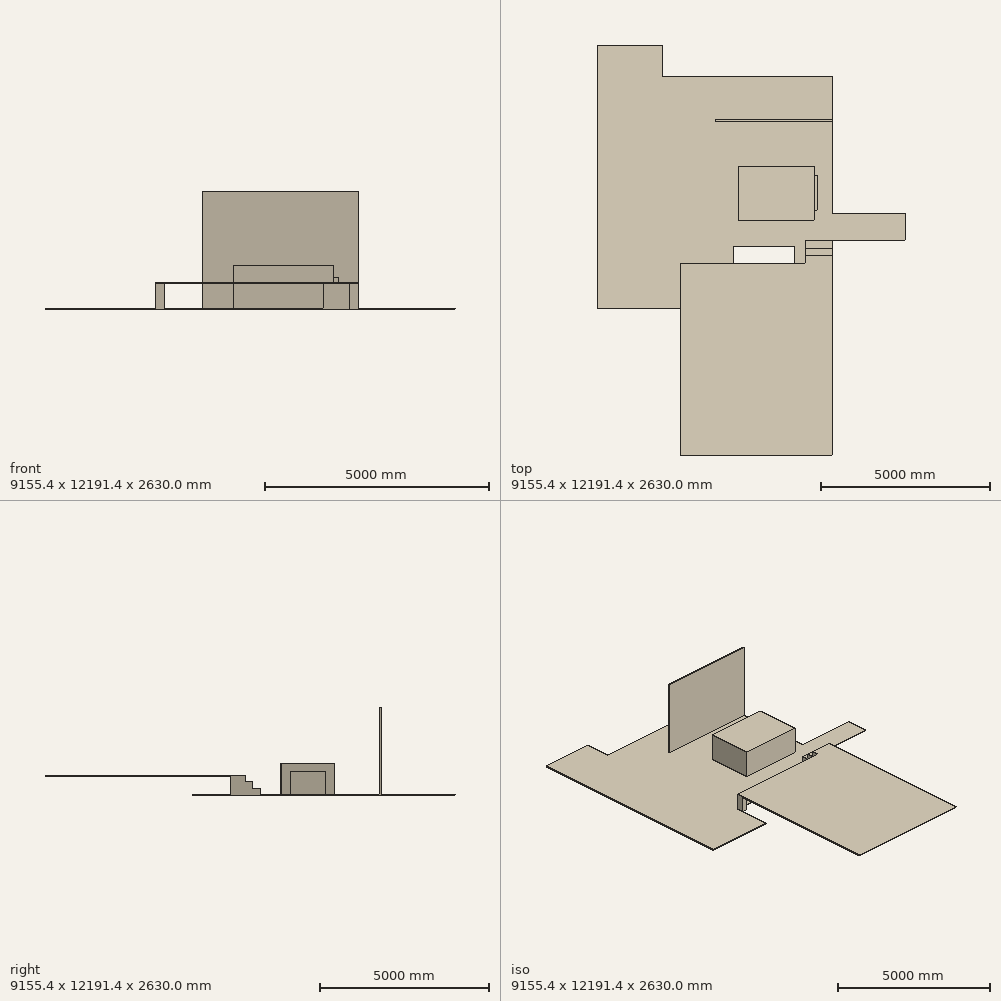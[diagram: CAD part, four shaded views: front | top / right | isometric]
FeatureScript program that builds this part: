
annotation { "Feature Type Name" : "Feature", "Feature Type Description" : "" }
export const myFeature = defineFeature(function(context is Context, id is Id, definition is map)
    precondition{}
    {
        {
            var Q0;
            Q0=qCreatedBy(makeId("Top.planeOp"),FACE);
            var sketch = newSketch(context, id + "F0", { "sketchPlane" : qUnion([Q0])});
            skLineSegment(sketch, "E0.bottom", {"start": v(-1125, 800) * mm, "end": v(1125, 800) * mm});
            skLineSegment(sketch, "E0.top", {"start": v(-1125, -800) * mm, "end": v(1125, -800) * mm});
            skLineSegment(sketch, "E0.left", {"start": v(-1125, 800) * mm, "end": v(-1125, -800) * mm});
            skLineSegment(sketch, "E0.right", {"start": v(1125, 800) * mm, "end": v(1125, -800) * mm});
            skPoint(sketch, "E0.middle", {"position": v(0, 0) * mm});
            skLineSegment(sketch, "E1.bottom", {"start": v(3.09, 2130) * mm, "end": v(-1796.91, 2130) * mm});
            skLineSegment(sketch, "E2", {"start": v(1675, 3460) * mm, "end": v(1675, -610) * mm});
            skLineSegment(sketch, "E3", {"start": v(1675, -610) * mm, "end": v(3053.14, -610) * mm});
            skLineSegment(sketch, "E4", {"start": v(3053.14, -610) * mm, "end": v(3053.14, 361.12) * mm});
            skLineSegment(sketch, "E5", {"start": v(3053.14, 361.12) * mm, "end": v(3843.14, 361.12) * mm});
            skLineSegment(sketch, "E6", {"start": v(3843.14, -1400) * mm, "end": v(2516.8, -1400) * mm});
            skLineSegment(sketch, "E7", {"start": v(2516.8, -1400) * mm, "end": v(2516.8, -3015.82) * mm});
            skLineSegment(sketch, "E8", {"start": v(2516.8, -3015.82) * mm, "end": v(1817.51, -3015.82) * mm});
            skLineSegment(sketch, "E9", {"start": v(1817.51, -3015.82) * mm, "end": v(1817.51, -1400) * mm});
            skLineSegment(sketch, "E10", {"start": v(1817.51, -1400) * mm, "end": v(1675, -1400) * mm});
            skLineSegment(sketch, "E11", {"start": v(1675, -1400) * mm, "end": v(1675, -2100) * mm});
            skLineSegment(sketch, "E12", {"start": v(1675, -2100) * mm, "end": v(885, -2100) * mm});
            skLineSegment(sketch, "E13", {"start": v(885, -2100) * mm, "end": v(885, -1400) * mm});
            skLineSegment(sketch, "E14", {"start": v(885, -2100) * mm, "end": v(-2855.91, -2100) * mm});
            skLineSegment(sketch, "E15", {"start": v(885, -1400) * mm, "end": v(1675, -1400) * mm});
            skLineSegment(sketch, "E16", {"start": v(1675, -1400) * mm, "end": v(1675, -1400) * mm});
            skLineSegment(sketch, "E17.bottom", {"start": v(-2855.91, -300) * mm, "end": v(-2355.91, -300) * mm});
            skLineSegment(sketch, "E17.top", {"start": v(-2855.91, -2100) * mm, "end": v(-2355.91, -2100) * mm});
            skLineSegment(sketch, "E17.left", {"start": v(-2855.91, -300) * mm, "end": v(-2855.91, -2100) * mm});
            skLineSegment(sketch, "E17.right", {"start": v(-2355.91, -300) * mm, "end": v(-2355.91, -2100) * mm});
            skLineSegment(sketch, "E18", {"start": v(2516.8, -1400) * mm, "end": v(1817.51, -1400) * mm});
            skLineSegment(sketch, "E19", {"start": v(3053.14, -610) * mm, "end": v(3843.14, -610) * mm});
            skLineSegment(sketch, "E20", {"start": v(3843.14, 361.12) * mm, "end": v(3843.14, -610) * mm});
            skLineSegment(sketch, "E21", {"start": v(3843.14, -610) * mm, "end": v(3843.14, -1400) * mm});
            skLineSegment(sketch, "E22", {"start": v(-2855.91, -2100) * mm, "end": v(-2855.91, -3422.45) * mm});
            skLineSegment(sketch, "E23", {"start": v(-2855.91, -3422.45) * mm, "end": v(-2855.91, -7802.65) * mm});
            skLineSegment(sketch, "E24", {"start": v(-2855.91, -7802.65) * mm, "end": v(1675, -7802.65) * mm});
            skLineSegment(sketch, "E25", {"start": v(1675, -7802.65) * mm, "end": v(1675, -2100) * mm});
            skLineSegment(sketch, "E26", {"start": v(-2855.91, -3422.45) * mm, "end": v(-5312.24, -3422.45) * mm});
            skLineSegment(sketch, "E27", {"start": v(-3375.14, 3460) * mm, "end": v(1675, 3460) * mm});
            skLineSegment(sketch, "E28.bottom", {"start": v(-1185.34, -3222.94) * mm, "end": v(110.16, -3222.94) * mm});
            skLineSegment(sketch, "E28.top", {"start": v(-1185.34, -6783.92) * mm, "end": v(110.16, -6783.92) * mm});
            skLineSegment(sketch, "E28.left", {"start": v(-1185.34, -3222.94) * mm, "end": v(-1185.34, -6783.92) * mm});
            skLineSegment(sketch, "E28.right", {"start": v(110.16, -3222.94) * mm, "end": v(110.16, -6783.92) * mm});
            skLineSegment(sketch, "E29.bottom", {"start": v(1675, 2130) * mm, "end": v(-1796.91, 2130) * mm});
            skLineSegment(sketch, "E29.top", {"start": v(1675, 2180) * mm, "end": v(-1796.91, 2180) * mm});
            skLineSegment(sketch, "E29.left", {"start": v(1675, 2130) * mm, "end": v(1675, 2180) * mm});
            skLineSegment(sketch, "E30", {"start": v(-1796.91, 2130) * mm, "end": v(-1796.91, 2180) * mm});
            skLineSegment(sketch, "E31", {"start": v(-3375.14, 3460) * mm, "end": v(-3375.14, 4402.44) * mm});
            skLineSegment(sketch, "E32", {"start": v(-3366, 4388.7) * mm, "end": v(-5312.24, 4388.7) * mm});
            skLineSegment(sketch, "E33", {"start": v(-5312.24, -3422.45) * mm, "end": v(-5312.24, 4388.7) * mm});
            skLineSegment(sketch, "E34.bottom", {"start": v(544.09, -2100) * mm, "end": v(-1255.91, -2100) * mm});
            skLineSegment(sketch, "E34.top", {"start": v(544.09, -1600) * mm, "end": v(-1255.91, -1600) * mm});
            skLineSegment(sketch, "E34.left", {"start": v(544.09, -2100) * mm, "end": v(544.09, -1600) * mm});
            skLineSegment(sketch, "E34.right", {"start": v(-1255.91, -2100) * mm, "end": v(-1255.91, -1600) * mm});
            skSolve(sketch);
        }
        {
            var Q0;
            Q0=makeQuery(id+"F0.imprint","IMPRINT",FACE,{"disambiguationData":[TD([[makeQuery(id+"F0.imprint","IMPRINT",EDGE,{"derivedFrom":sQuery(id+"F0.wireOp",EDGE,"E0.bottom")}),-1.0]])]});
            extrude(context, id + "F1", {"entities" : qUnion([Q0]), "depth" : 940 * mm});
        }
        {
            var Q0;
            Q0=makeQuery(id+"F0.imprint","IMPRINT",FACE,{"disambiguationData":[TD([[makeQuery(id+"F0.imprint","IMPRINT",EDGE,{"derivedFrom":sQuery(id+"F0.wireOp",EDGE,"E0.bottom")}),1.0]])]});
            var Q1;
            Q1=makeQuery(id+"F0.imprint","IMPRINT",FACE,{"disambiguationData":[TD([[makeQuery(id+"F0.imprint","IMPRINT",EDGE,{"derivedFrom":sQuery(id+"F0.wireOp",EDGE,"E1.top")}),-1.0]])]});
            var Q2;
            Q2=makeQuery(id+"F0.imprint","IMPRINT",FACE,{"disambiguationData":[TD([[makeQuery(id+"F0.imprint","IMPRINT",EDGE,{"derivedFrom":sQuery(id+"F0.wireOp",EDGE,"E17.bottom")}),-1.0]])]});
            var Q3;
            Q3=makeQuery(id+"F0.imprint","IMPRINT",FACE,{"disambiguationData":[TD([[makeQuery(id+"F0.imprint","IMPRINT",EDGE,{"derivedFrom":sQuery(id+"F0.wireOp",EDGE,"E11")}),-1.0]])]});
            var Q4;
            Q4=makeQuery(id+"F0.imprint","IMPRINT",FACE,{"disambiguationData":[TD([[makeQuery(id+"F0.imprint","IMPRINT",EDGE,{"derivedFrom":sQuery(id+"F0.wireOp",EDGE,"H7tPlg6k-jWhV-1Bwv-etl5-hqIqn9BFFYRF.bottom")}),1.0]])]});
            var Q5;
            Q5=makeQuery(id+"F0.imprint","IMPRINT",FACE,{"disambiguationData":[TD([[makeQuery(id+"F0.imprint","IMPRINT",EDGE,{"derivedFrom":sQuery(id+"F0.wireOp",EDGE,"qLvadJ40-6Qau-X74K-FQ8g-niZacNmFLS0U.bottom")}),1.0]])]});
            var Q6;
            Q6=makeQuery(id+"F0.imprint","IMPRINT",FACE,{"disambiguationData":[TD([[makeQuery(id+"F0.imprint","IMPRINT",EDGE,{"derivedFrom":sQuery(id+"F0.wireOp",EDGE,"E29.top")}),1.0]])]});
            var Q7;
            Q7=makeQuery(id+"F0.imprint","IMPRINT",FACE,{"disambiguationData":[TD([[makeQuery(id+"F0.imprint","IMPRINT",EDGE,{"derivedFrom":sQuery(id+"F0.wireOp",EDGE,"E0.bottom")}),-1.0]])]});
            var Q8;
            Q8=makeQuery(id+"F0.imprint","IMPRINT",FACE,{"disambiguationData":[TD([[makeQuery(id+"F0.imprint","IMPRINT",EDGE,{"derivedFrom":sQuery(id+"F0.wireOp",EDGE,"E34.bottom")}),-1.0]])]});
            extrude(context, id + "F2", {"entities" : qUnion([Q0, Q1, Q2, Q3, Q4, Q5, Q6, Q7, Q8]), "operationType" : NewBodyOperationType.ADD, "oppositeDirection" : true, "depth" : 30 * mm});
        }
        {
            var Q0;
            Q0=makeQuery(id+"F1.opExtrude","SWEPT_FACE",FACE,{"disambiguationData":[OSD([sQuery(id+"F0.wireOp",EDGE,"E0.right")])]});
            var sketch = newSketch(context, id + "F3", { "sketchPlane" : qUnion([Q0])});
            skLineSegment(sketch, "E35.bottom", {"start": v(-525, 0) * mm, "end": v(525, 0) * mm});
            skLineSegment(sketch, "E35.top", {"start": v(-525, 690) * mm, "end": v(525, 690) * mm});
            skLineSegment(sketch, "E35.left", {"start": v(-525, 0) * mm, "end": v(-525, 690) * mm});
            skLineSegment(sketch, "E35.right", {"start": v(525, 0) * mm, "end": v(525, 690) * mm});
            skPoint(sketch, "E36", {"position": v(0, 690) * mm});
            skSolve(sketch);
        }
        {
            var Q0;
            Q0=qSketchRegion(id+"F3",true);
            extrude(context, id + "F4", {"entities" : qUnion([Q0]), "operationType" : NewBodyOperationType.ADD, "depth" : 100 * mm});
        }
        {
            var Q0;
            Q0=makeQuery(id+"F0.imprint","IMPRINT",FACE,{"disambiguationData":[TD([[makeQuery(id+"F0.imprint","IMPRINT",EDGE,{"derivedFrom":sQuery(id+"F0.wireOp",EDGE,"E29.top")}),1.0]])]});
            extrude(context, id + "F5", {"entities" : qUnion([Q0]), "operationType" : NewBodyOperationType.ADD, "depth" : 2600 * mm});
        }
        {
            var Q0;
            Q0=makeQuery(id+"F2.opExtrude","CAP_FACE",FACE,{"disambiguationData":[OSD([sQuery(id+"F0.wireOp",EDGE,"E2"),sQuery(id+"F0.wireOp",EDGE,"E3"),sQuery(id+"F0.wireOp",EDGE,"E6"),sQuery(id+"F0.wireOp",EDGE,"E10"),sQuery(id+"F0.wireOp",EDGE,"E11"),sQuery(id+"F0.wireOp",EDGE,"E12"),sQuery(id+"F0.wireOp",EDGE,"E14"),sQuery(id+"F0.wireOp",EDGE,"E17.top"),sQuery(id+"F0.wireOp",EDGE,"E18"),sQuery(id+"F0.wireOp",EDGE,"E19"),sQuery(id+"F0.wireOp",EDGE,"E21"),sQuery(id+"F0.wireOp",EDGE,"E22"),sQuery(id+"F0.wireOp",EDGE,"E26"),sQuery(id+"F0.wireOp",EDGE,"BivDKwDv-rJwD-EJ6L-Itse-b2Q6de9G2O9e"),sQuery(id+"F0.wireOp",EDGE,"GaEvWnw7-THx7-ogP4-HRQ5-eutlSQDa1YNG"),sQuery(id+"F0.wireOp",EDGE,"ROQ74bbm-dzdB-rij4-2ZSW-2immjU0JxgkO"),sQuery(id+"F0.wireOp",EDGE,"E27"),sQuery(id+"F0.wireOp",EDGE,"E29.left")])],"isStart":false});
            var sketch = newSketch(context, id + "F6", { "sketchPlane" : qUnion([Q0])});
            skLineSegment(sketch, "E37.bottom", {"start": v(-2855.91, 2100) * mm, "end": v(-2655.91, 2100) * mm});
            skLineSegment(sketch, "E37.top", {"start": v(-2855.91, 2300) * mm, "end": v(-2655.91, 2300) * mm});
            skLineSegment(sketch, "E37.left", {"start": v(-2855.91, 2100) * mm, "end": v(-2855.91, 2300) * mm});
            skLineSegment(sketch, "E37.right", {"start": v(-2655.91, 2100) * mm, "end": v(-2655.91, 2300) * mm});
            skLineSegment(sketch, "E38.bottom", {"start": v(1675, 2100) * mm, "end": v(1475, 2100) * mm});
            skLineSegment(sketch, "E38.top", {"start": v(1675, 2300) * mm, "end": v(1475, 2300) * mm});
            skLineSegment(sketch, "E38.left", {"start": v(1675, 2100) * mm, "end": v(1675, 2300) * mm});
            skLineSegment(sketch, "E38.right", {"start": v(1475, 2100) * mm, "end": v(1475, 2300) * mm});
            skSolve(sketch);
        }
        {
            var Q0;
            Q0=qSketchRegion(id+"F6",true);
            var Q1;
            Q1=makeQuery(id+"F6.imprint","IMPRINT",FACE,{"disambiguationData":[TD([[makeQuery(id+"F6.imprint","IMPRINT",EDGE,{"derivedFrom":makeQuery(id+"F2.opExtrude","CAP_EDGE",EDGE,{"disambiguationData":[OSD([sQuery(id+"F0.wireOp",EDGE,"J4IDLds2-xMvC-BjQL-q1XK-hAskijoe9bhO")])],"isStart":false})}),1.0]])]});
            extrude(context, id + "F7", {"entities" : qUnion([Q0, Q1]), "operationType" : NewBodyOperationType.ADD, "oppositeDirection" : true, "depth" : 600 * mm});
        }
        {
            var Q0;
            Q0=makeQuery(id+"F7.opExtrude","CAP_FACE",FACE,{"disambiguationData":[OSD([sQuery(id+"F6.wireOp",EDGE,"E37.bottom"),sQuery(id+"F6.wireOp",EDGE,"E37.top"),sQuery(id+"F6.wireOp",EDGE,"E37.left"),sQuery(id+"F6.wireOp",EDGE,"E37.right")])],"isStart":false});
            var sketch = newSketch(context, id + "F8", { "sketchPlane" : qUnion([Q0])});
            skLineSegment(sketch, "E39.0.0", {"start": v(1675, -7802.65) * mm, "end": v(1675, -2100) * mm});
            skLineSegment(sketch, "E39.0.1", {"start": v(1675, -2100) * mm, "end": v(885, -2100) * mm});
            skLineSegment(sketch, "E39.0.2", {"start": v(885, -2100) * mm, "end": v(885, -2100) * mm});
            skLineSegment(sketch, "E39.0.3", {"start": v(885, -2100) * mm, "end": v(885, -2100) * mm});
            skLineSegment(sketch, "E39.0.4", {"start": v(885, -2100) * mm, "end": v(885, -2100) * mm});
            skLineSegment(sketch, "E39.0.5", {"start": v(885, -2100) * mm, "end": v(885, -2100) * mm});
            skLineSegment(sketch, "E39.0.6", {"start": v(885, -2100) * mm, "end": v(544.09, -2100) * mm});
            skLineSegment(sketch, "E39.0.7", {"start": v(544.09, -2100) * mm, "end": v(-2855.91, -2100) * mm});
            skLineSegment(sketch, "E39.0.8", {"start": v(-2855.91, -2100) * mm, "end": v(-2855.91, -3422.45) * mm});
            skLineSegment(sketch, "E39.0.9", {"start": v(-2855.91, -3422.45) * mm, "end": v(-2855.91, -7802.65) * mm});
            skLineSegment(sketch, "E39.0.10", {"start": v(-2855.91, -7802.65) * mm, "end": v(1675, -7802.65) * mm});
            skSolve(sketch);
        }
        {
            var Q0;
            Q0=qSketchRegion(id+"F8",true);
            extrude(context, id + "F9", {"entities" : qUnion([Q0]), "operationType" : NewBodyOperationType.ADD, "oppositeDirection" : true, "depth" : 30 * mm});
        }
        {
            var Q0;
            Q0=makeQuery(id+"F9.boolean.opBoolean","MERGE",FACE,{"derivedFrom":[makeQuery(id+"F7.boolean.opBoolean","MERGE",FACE,{"derivedFrom":[makeQuery(id+"F2.opExtrude","SWEPT_FACE",FACE,{"disambiguationData":[OSD([sQuery(id+"F0.wireOp",EDGE,"E11")])]}),makeQuery(id+"F7.opExtrude","SWEPT_FACE",FACE,{"disambiguationData":[OSD([sQuery(id+"F6.wireOp",EDGE,"E38.left")])]})]}),makeQuery(id+"F9.opExtrude","SWEPT_FACE",FACE,{"disambiguationData":[OSD([sQuery(id+"F8.wireOp",EDGE,"E39.0.0")])]})]});
            var sketch = newSketch(context, id + "F10", { "sketchPlane" : qUnion([Q0])});
            skLineSegment(sketch, "E40", {"start": v(-2100, 570) * mm, "end": v(-1866.67, 570) * mm});
            skLineSegment(sketch, "E41", {"start": v(-1866.67, 570) * mm, "end": v(-1866.67, 380) * mm});
            skLineSegment(sketch, "E42", {"start": v(-1866.67, 380) * mm, "end": v(-1633.33, 380) * mm});
            skLineSegment(sketch, "E43", {"start": v(-1633.33, 380) * mm, "end": v(-1633.33, 190) * mm});
            skLineSegment(sketch, "E44", {"start": v(-1633.33, 190) * mm, "end": v(-1400, 190) * mm});
            skLineSegment(sketch, "E45", {"start": v(-1400, 190) * mm, "end": v(-1400, 0) * mm});
            skLineSegment(sketch, "E46", {"start": v(-1400, 0) * mm, "end": v(-2100, 0) * mm});
            skLineSegment(sketch, "E47", {"start": v(-2100, 0) * mm, "end": v(-2100, 570) * mm});
            skSolve(sketch);
        }
        {
            var Q0;
            Q0=qSketchRegion(id+"F10",true);
            var Q1;
            Q1=sQuery(id+"F0.wireOp",VERTEX,"E13.end");
            extrude(context, id + "F11", {"entities" : qUnion([Q0]), "operationType" : NewBodyOperationType.ADD, "endBound" : BoundingType.UP_TO_VERTEX, "oppositeDirection" : true, "endBoundEntityVertex" : qUnion([Q1]), "depth" : 25 * mm});
        }
    });
